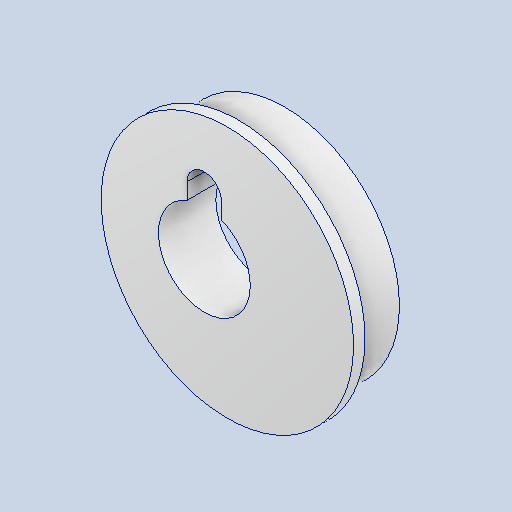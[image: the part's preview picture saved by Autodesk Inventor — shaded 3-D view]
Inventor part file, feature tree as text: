
AUTODESK INVENTOR PART (.ipt)
format: ipt  version: 2024 (Build 280153000, 153)  size: 143,360 bytes
history: native  units: mm
features: sketch x4, extrude x3, other x1, hole x1, projected_geometry x1
ambient origin geometry x8: Origin, YZ Plane, XZ Plane, XY Plane, X Axis, Y Axis, Z Axis, Center Point
bodies: Body1 (feature_tree)
feature tree (10):
  other  "ソリッド1"
  extrude  "押し出し1"  Depth=20.0mm
  extrude  "押し出し2"  Depth=5.0mm TaperAngle=0.0deg
  hole  "穴1"  [1 undecoded]
  extrude  "押し出し3"  Depth=1.0mm TaperAngle=0.0deg
  sketch  "スケッチ1"
  sketch  "スケッチ2"
  projected_geometry  "投影ループ1"
  sketch  "スケッチ3"
  sketch  "スケッチ4"
note: 1 required parameter value undecoded (feature->parameter linkage not recoverable at this tier; creation-order binding heuristic only, values carry confidence <= 0.55)
